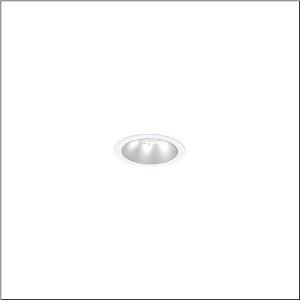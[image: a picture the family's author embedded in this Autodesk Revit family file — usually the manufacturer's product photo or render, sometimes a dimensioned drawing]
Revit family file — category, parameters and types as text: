
# Revit family: lunis_21_s_51db19ma91c
name_source: partatom
category: Lighting Fixtures
units: mm (PartAtom-declared; Revit-internal decimal feet)

## family parameters
Cut with Voids When Loaded = No
Host = Face
Light Source = No
Part Type = Normal
Room Calculation Point = No
Round Connector Dimension = Use Diameter
Shared = No

## types (1)
- --- (1 x LED, 930 lm, 5.9 W, 6500K)
    Apparent Load = 6 VA
    CIE Flux Codes = 90 98 100 100 100
    Color Rendering = 80
    Color Temperature = 6500K
    Default Elevation = 1800 mm
    Description = Lunis 21,  S, downlight, light control with lens, of PMMA, anti glare with reflector, of PC, matt, light emission: direct distribution, LED rated luminous flux: 940lm, light colour: 830/840/865, with terminal, 3-pole, mains connection: 220..240V, AC, 50..60Hz, housing, round, of diecast aluminium, traffic white (RAL 9016), diameter: 84mm, clamping range: 1..40mm, protection rating (complete): IP20, protection rating (on room side): IP54, insulation class (complete): insulation class II (safety insulation), certification: CE, impact resistance: IK03, packaging unit: 1 piece
    Height = 0 mm  [stored 0 ft]
    Lamp = 1 x LED
    Lamp Light Flux = 930 lm
    Lamp Power = 5.9 W
    Lamp count = 1
    Length = 84 mm
    Luminous efficacy = 158 lm/W
    Manufacturer = Siteco
    ModVariant = No
    Model = 51DB19MA91C
    Mounting Place = Ceiling
    Mounting Type = Recessed
    Number of Poles = 1
    OnlyDefault = Yes
    Power Factor = 1
    Product Name = Lunis 21 S
    Product group = downlight
    ProductGroupID = 401
    Protection Class = Protection class II
    Protection Degree = IP 20
    RLX_Detail_Level = 1
    RLX_Emergency_Light_Flux = 0 lm
    RLX_Emergency_Type = 0
    RLX_Emergency_Type_DB = No
    RlxData = <blob elided: 8577 chars, md5=338d624b>
    Socket = socket
    Standby Power = 0 W
    System Light Flux = 930 lm
    System Power = 6 W
    Type Comments = individual setting: colour temperature 6500K
    Type Image = l_1290846.jpg
    URL = http://relux.com
    VarID = @adj_039201
    Voltage = 0 V
    Weight = 0.00 kg
    Width = 0 mm  [stored 0 ft]

note: [stored X ft] marks values corroborated as IEEE doubles in the binary element streams (Revit-internal decimal feet)

## geometry (parser evidence)
native form markers: Sweep x9
no freeform markers — native parametric forms only
